# Revit family: MIREL-L LED M600Q
name_source: partatom
category: Lighting Fixtures
revit_build: Autodesk Revit 2014 (Build: 20140709_2115(x64)
units: mm (PartAtom-declared; Revit-internal decimal feet)

## types (1)
- MIREL-L NIV LED3800-840 M600Q LDO
    Apparent Load = 29 VA
    Assembly Code = D5020200
    Color Filter = 16777215
    Default Elevation = 0 mm  [stored 0 ft]
    Description = Recessed LED luminaire
    Dimming Lamp Color Temperature Shift = <None>
    Emit Shape Visible in Rendering = No
    Emit from Rectangle Length = 598 mm  [stored 1.96194 ft]
    Emit from Rectangle Width = 598 mm  [stored 1.96194 ft]
    Height = 74 mm  [stored 0.242782 ft]
    Lamp = LED
    Length = 598 mm  [stored 1.96194 ft]
    Manufacturer = Zumtobel Lighting
    Model = 42925926
    Photometric Web File = 42925926_(STD_LEO).IES
    Tilt Angle = 90.00°
    URL = http://www.zumtobel.com
    Voltage = 230 V
    Width = 598 mm  [stored 1.96194 ft]

note: [stored X ft] marks values corroborated as IEEE doubles in the binary element streams (Revit-internal decimal feet)

## geometry (parser evidence)
native form markers: Sweep x5
no freeform markers — native parametric forms only
